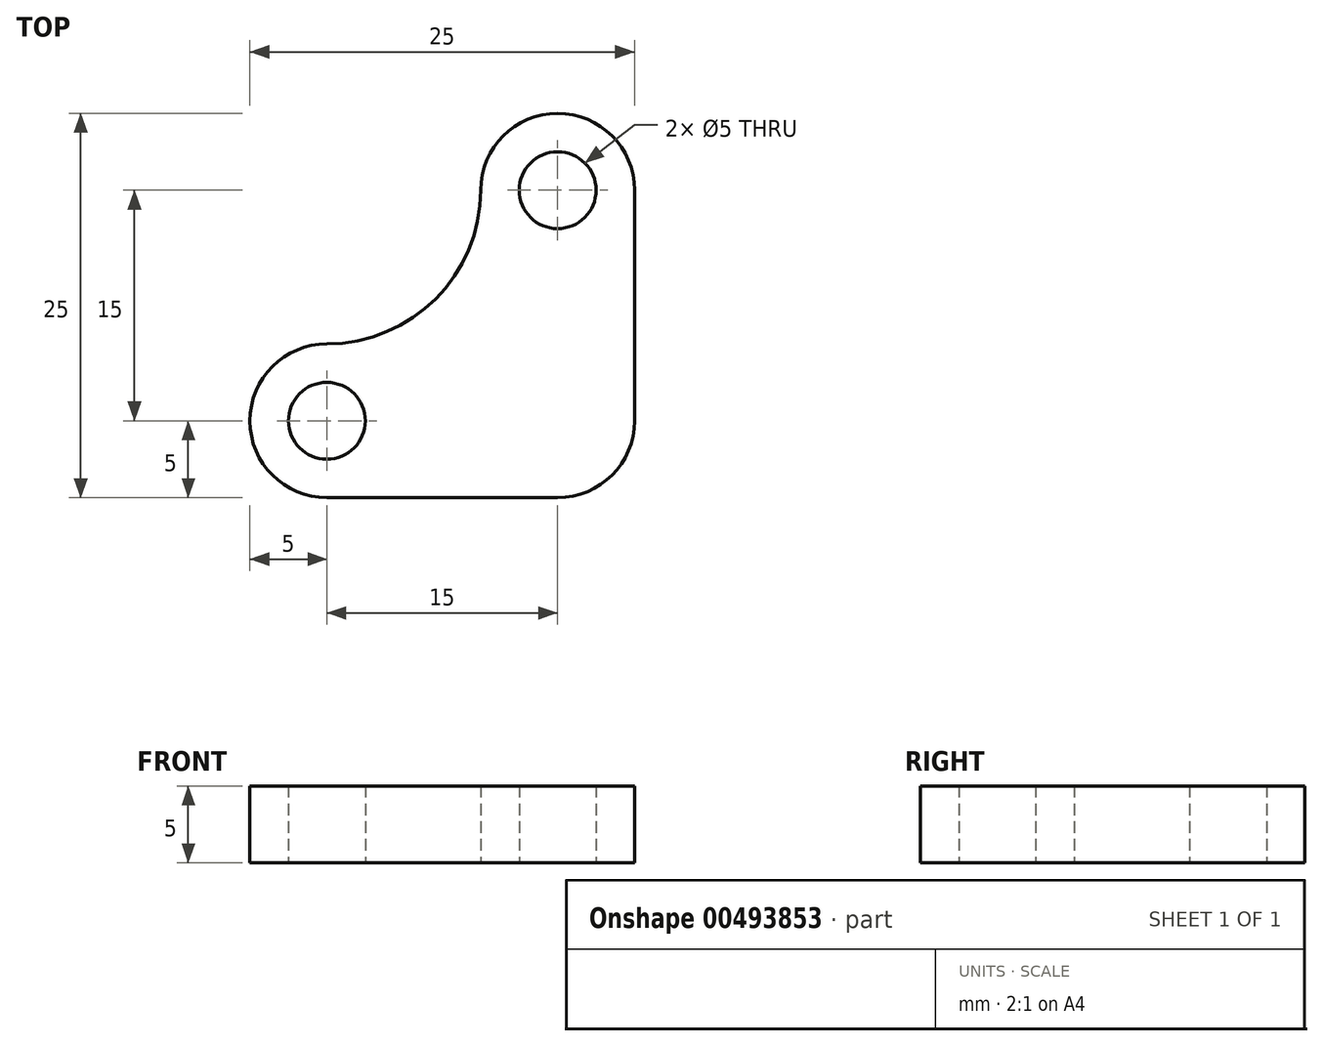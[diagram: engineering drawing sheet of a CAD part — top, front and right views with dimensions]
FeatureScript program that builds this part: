
annotation { "Feature Type Name" : "Feature", "Feature Type Description" : "" }
export const myFeature = defineFeature(function(context is Context, id is Id, definition is map)
    precondition{}
    {
        {
            var Q0;
            Q0=qCreatedBy(makeId("Top.planeOp"),FACE);
            var sketch = newSketch(context, id + "F0", { "sketchPlane" : qUnion([Q0])});
            skArc(sketch, "E0", {"start": v(5, 15) * mm, "mid": v(0, 20) * mm, "end": v(-5, 15) * mm});
            skArc(sketch, "E1", {"start": v(0, -5) * mm, "mid": v(3.54, -3.54) * mm, "end": v(5, 0) * mm});
            skArc(sketch, "E2", {"start": v(-15, 5) * mm, "mid": v(-20, 0) * mm, "end": v(-15, -5) * mm});
            skArc(sketch, "E3", {"start": v(-15, 5) * mm, "mid": v(-7.93, 7.93) * mm, "end": v(-5, 15) * mm});
            skLineSegment(sketch, "E4.top", {"start": v(-15, -5) * mm, "end": v(0, -5) * mm});
            skLineSegment(sketch, "E4.right", {"start": v(5, 15) * mm, "end": v(5, 0) * mm});
            skLineSegment(sketch, "E5.trimOffspring", {"start": v(-15, 0) * mm, "end": v(-15, -5) * mm});
            skCircle(sketch, "E6", {"center": v(-15, 0) * mm, "radius": 2.5 * mm});
            skCircle(sketch, "E7", {"center": v(0, 15) * mm, "radius": 2.5 * mm});
            skSolve(sketch);
        }
        {
            var Q0;
            Q0 = qSketchRegion(id + "F0", true);
            extrude(context, id + "F1", {"entities" : qUnion([Q0]), "depth" : 5 * mm});
        }
    });
